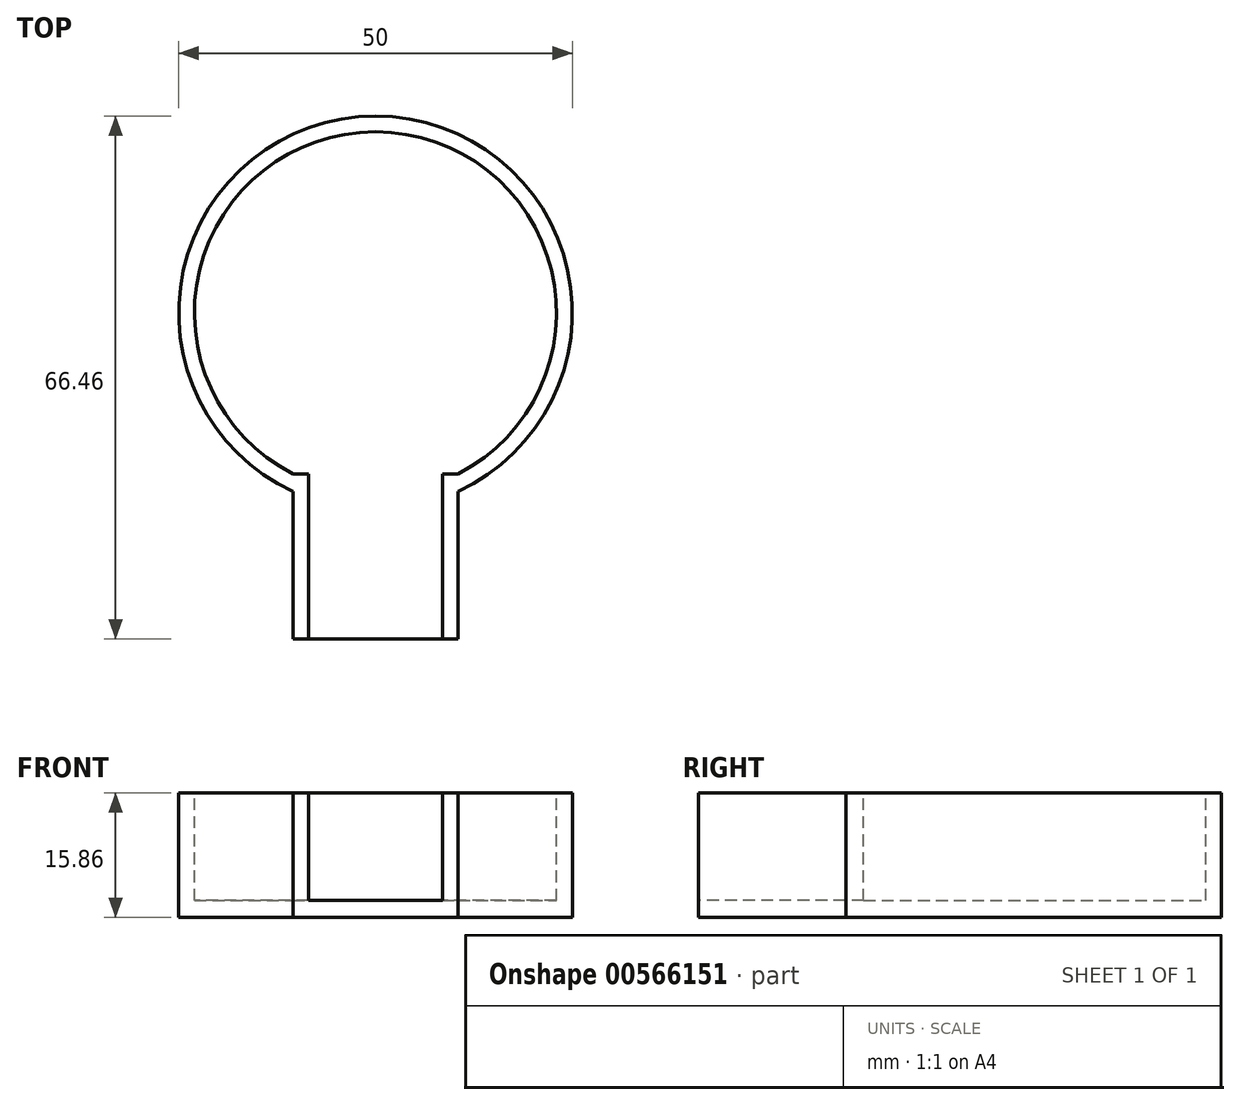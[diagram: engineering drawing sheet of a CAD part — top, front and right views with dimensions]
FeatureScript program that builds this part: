
annotation { "Feature Type Name" : "Feature", "Feature Type Description" : "" }
export const myFeature = defineFeature(function(context is Context, id is Id, definition is map)
    precondition{}
    {
        {
            var Q0;
            Q0=qCreatedBy(makeId("Top.planeOp"),FACE);
            var sketch = newSketch(context, id + "F0", { "sketchPlane" : qUnion([Q0])});
            skCircle(sketch, "E0", {"center": v(0, 0) * mm, "radius": 25 * mm});
            skSolve(sketch);
        }
        {
            var Q0;
            Q0=makeQuery(id+"F0.imprint","IMPRINT",FACE,{"disambiguationData":[TD([[makeQuery(id+"F0.imprint","IMPRINT",EDGE,{"derivedFrom":sQuery(id+"F0.wireOp",EDGE,"E0")}),1.0]])]});
            extrude(context, id + "F1", {"entities" : qUnion([Q0]), "depth" : 15.86 * mm, "offsetDistance" : 25 * mm});
        }
        {
            var Q0;
            Q0=makeQuery(id+"F1.opExtrude","CAP_FACE",FACE,{"disambiguationData":[OSD([sQuery(id+"F0.wireOp",EDGE,"E0")])],"isStart":false});
            var sketch = newSketch(context, id + "F2", { "sketchPlane" : qUnion([Q0])});
            skCircle(sketch, "E1", {"center": v(0, 0) * mm, "radius": 23 * mm});
            skSolve(sketch);
        }
        {
            var Q0;
            Q0 = qSketchRegion(id + "F2", true);
            extrude(context, id + "F3", {"entities" : qUnion([Q0]), "operationType" : NewBodyOperationType.REMOVE, "oppositeDirection" : true, "depth" : 13.7 * mm, "offsetDistance" : 25 * mm});
        }
        {
            var Q0;
            Q0=qCreatedBy(makeId("Top.planeOp"),FACE);
            var sketch = newSketch(context, id + "F4", { "sketchPlane" : qUnion([Q0])});
            skLineSegment(sketch, "E2.bottom", {"start": v(10.5, -41.46) * mm, "end": v(-10.5, -41.46) * mm});
            skLineSegment(sketch, "E2.top", {"start": v(10.5, -20.46) * mm, "end": v(-10.5, -20.46) * mm});
            skLineSegment(sketch, "E2.left", {"start": v(10.5, -41.46) * mm, "end": v(10.5, -20.46) * mm});
            skLineSegment(sketch, "E2.right", {"start": v(-10.5, -41.46) * mm, "end": v(-10.5, -20.46) * mm});
            skPoint(sketch, "E2.middle", {"position": v(0, -30.96) * mm});
            skSolve(sketch);
        }
        {
            var Q0;
            Q0 = qSketchRegion(id + "F4", true);
            var Q1;
            Q1=makeQuery(id+"F1.opExtrude","CAP_FACE",FACE,{"disambiguationData":[OSD([sQuery(id+"F0.wireOp",EDGE,"E0")])],"isStart":false});
            extrude(context, id + "F5", {"entities" : qUnion([Q0]), "operationType" : NewBodyOperationType.ADD, "endBound" : BoundingType.UP_TO_SURFACE, "depth" : 25 * mm, "endBoundEntityFace" : qUnion([Q1]), "offsetDistance" : 25 * mm});
        }
        {
            var Q0;
            {var subQ0=sQuery(id+"F0.wireOp",EDGE,"E0");Q0=makeQuery(id+"F5.boolean.opBoolean","MERGE",FACE,{"derivedFrom":[makeQuery(id+"F1.opExtrude","CAP_FACE",FACE,{"disambiguationData":[OSD([subQ0])],"isStart":false}),makeQuery(id+"F5.opExtrude","CAP_FACE",FACE,{"disambiguationData":[OSD([subQ0])],"isStart":false})]});}
            var sketch = newSketch(context, id + "F6", { "sketchPlane" : qUnion([Q0])});
            skLineSegment(sketch, "E3.bottom", {"start": v(8.5, -42.64) * mm, "end": v(-8.5, -42.64) * mm});
            skLineSegment(sketch, "E3.top", {"start": v(8.5, -15.62) * mm, "end": v(-8.5, -15.62) * mm});
            skLineSegment(sketch, "E3.left", {"start": v(8.5, -42.64) * mm, "end": v(8.5, -15.62) * mm});
            skLineSegment(sketch, "E3.right", {"start": v(-8.5, -42.64) * mm, "end": v(-8.5, -15.62) * mm});
            skPoint(sketch, "E3.middle", {"position": v(0, -29.13) * mm});
            skSolve(sketch);
        }
        {
            var Q0;
            {var subQ0=sQuery(id+"F6.wireOp",EDGE,"E3.left");var subQ1=makeQuery(id+"F1.opExtrude","CAP_FACE",FACE,{"disambiguationData":[OSD([sQuery(id+"F0.wireOp",EDGE,"E0")])],"isStart":false});var subQ2=makeQuery(id+"F5.opExtrude","TWEAK_EDGE",EDGE,{"derivedFrom":[subQ1,makeQuery(id+"F4.imprint","IMPRINT",EDGE,{"derivedFrom":sQuery(id+"F4.wireOp",EDGE,"E2.bottom")})]});var subQ3=makeQuery(id+"F6.imprint","INTERSECT",VERTEX,{"derivedFrom":[subQ2,subQ0]});Q0=makeQuery(id+"F6.imprint","IMPRINT",FACE,{"disambiguationData":[TD([[makeQuery(id+"F6.imprint","IMPRINT",EDGE,{"disambiguationData":[TD([[subQ3,-1.0]])],"derivedFrom":subQ0}),1.0]])]});}
            var Q1;
            Q1=makeQuery(id+"F3.boolean.opBoolean","COPY",FACE,{"derivedFrom":makeQuery(id+"F3.opExtrude","CAP_FACE",FACE,{"disambiguationData":[OSD([sQuery(id+"F2.wireOp",EDGE,"E1")])],"isStart":false})});
            extrude(context, id + "F7", {"entities" : qUnion([Q0]), "operationType" : NewBodyOperationType.REMOVE, "endBound" : BoundingType.UP_TO_SURFACE, "oppositeDirection" : true, "depth" : 25 * mm, "endBoundEntityFace" : qUnion([Q1]), "offsetDistance" : 25 * mm});
        }
    });
